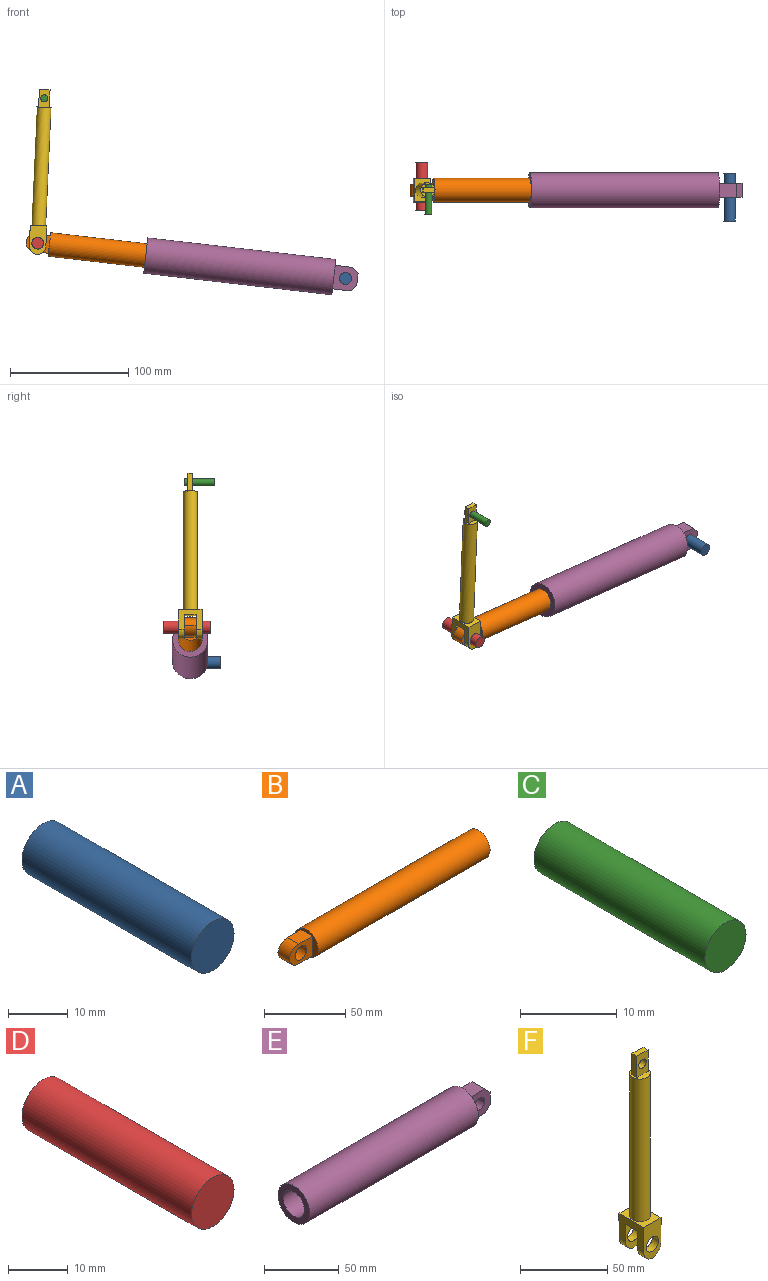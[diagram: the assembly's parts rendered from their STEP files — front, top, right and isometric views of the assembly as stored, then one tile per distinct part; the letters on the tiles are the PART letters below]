
ASSEMBLY  parts=6 mates=6
PART A: 3 faces, bbox 10x40x10 mm
  f0: cylinder r=5mm len=40mm, axis (0,1,0), area 1256.6mm2, adj f1,f2
  f1: plane 10x10mm, normal (0,-1,0), area 78.5mm2, adj f0
  f2: plane 10x10mm, normal (0,1,0), area 78.5mm2, adj f0
PART B: 10 faces, bbox 170x20x20 mm
  f0: plane 20x20mm, normal (-1,0,0), area 164.2mm2, adj f1,f3,f4,f5,f6
  f1: cylinder r=10mm len=150mm, axis (-1,0,0), area 9424.8mm2, adj f0,f2
  f2: plane 20x20mm, normal (1,0,0), area 314.2mm2, adj f1
  f3: plane 19.98x15mm, normal (0,-1,0), area 194mm2, adj f0,f4,f6,f7,f8,f9
  f4: plane 12x10mm, normal (0,0,1), area 120mm2, adj f0,f3,f5,f9
  f5: plane 19.98x15mm, normal (0,1,0), area 194mm2, adj f0,f4,f6,f7,f8,f9
  f6: plane 12x10mm, normal (0,0,-1), area 120mm2, adj f0,f3,f5,f8
  f7: cylinder r=5mm len=10mm, axis (0,-1,0), area 314.2mm2, adj f3,f5
  f8: cylinder r=8mm len=10mm, axis (0,1,0), area 120.7mm2, adj f3,f5,f6,f9
  f9: cylinder r=8mm len=10mm, axis (0,-1,0), area 120.7mm2, adj f3,f4,f5,f8
PART C: 3 faces, bbox 6x25x6 mm
  f0: cylinder r=3mm len=25mm, axis (0,1,0), area 471.2mm2, adj f1,f2
  f1: plane 6x6mm, normal (0,-1,0), area 28.3mm2, adj f0
  f2: plane 6x6mm, normal (0,1,0), area 28.3mm2, adj f0
PART D: 3 faces, bbox 10x40x10 mm
  f0: cylinder r=5mm len=40mm, axis (0,1,0), area 1256.6mm2, adj f1,f2
  f1: plane 10x10mm, normal (0,-1,0), area 78.5mm2, adj f0
  f2: plane 10x10mm, normal (0,1,0), area 78.5mm2, adj f0
PART E: 13 faces, bbox 180x30x30 mm
  f0: cylinder r=10mm len=150mm, axis (-1,0,0), area 9424.8mm2, adj f2,f3
  f1: cylinder r=15mm len=160mm, axis (-1,0,0), area 15079.6mm2, adj f2,f4
  f2: plane 30x30mm, normal (-1,0,0), area 392.7mm2, adj f0,f1
  f3: plane 20x20mm, normal (-1,0,0), area 314.2mm2, adj f0
  f4: plane 30x30mm, normal (1,0,0), area 466.9mm2, adj f1,f5,f6,f7,f8
  f5: plane 20x20mm, normal (0,-1,0), area 296.5mm2, adj f4,f6,f8,f9,f10,f11,f12
  f6: plane 15x12mm, normal (0,0,-1), area 180mm2, adj f4,f5,f7,f11
  f7: plane 20x20mm, normal (0,1,0), area 296.5mm2, adj f4,f6,f8,f9,f10,f11,f12
  f8: plane 15x12mm, normal (0,0,1), area 180mm2, adj f4,f5,f7,f12
  f9: plane 12x10mm, normal (1,0,0), area 120mm2, adj f5,f7,f11,f12
  f10: cylinder r=5mm len=12mm, axis (0,-1,0), area 377mm2, adj f5,f7
  f11: plane 12x5mm, normal (0.71,0,-0.71), area 84.9mm2, adj f5,f6,f7,f9
  f12: plane 12x5mm, normal (0.71,0,0.71), area 84.9mm2, adj f5,f7,f8,f9
PART F: 25 faces, bbox 14x20x139.9 mm
  f0: plane 12x12mm, normal (0,0,1), area 77.1mm2, adj f18,f19,f20,f21,f22
  f1: plane 19.94x14mm, normal (0,1,0), area 174mm2, adj f2,f4,f11,f13,f16,f17
  f2: plane 20.02x17mm, normal (-1,0,0), area 220.1mm2, adj f1,f3,f5,f7,f9,f10,f11,f14
  f3: plane 19.94x14mm, normal (0,-1,0), area 174mm2, adj f2,f4,f11,f13,f16,f17
  f4: plane 12x5mm, normal (1,0,0), area 60mm2, adj f1,f3,f11,f16
  f5: plane 24.94x14.03mm, normal (0,-1,0), area 244.2mm2, adj f2,f6,f8,f10,f11,f12,f14,f15
  f6: plane 12x5mm, normal (1,0,0), area 60mm2, adj f5,f7,f11,f15
  f7: plane 19.94x14mm, normal (0,1,0), area 174mm2, adj f2,f6,f11,f12,f14,f15
  f8: plane 20.02x5mm, normal (1,0,0), area 100.1mm2, adj f5,f9,f10,f11
  f9: plane 14.03x5mm, normal (0,1,0), area 70.2mm2, adj f2,f8,f10,f11
  f10: plane 20.02x14.03mm, normal (0,0,1), area 167.8mm2, adj f2,f5,f8,f9,f18
  f11: plane 20.02x14.03mm, normal (0,0,-1), area 140.9mm2, adj f1,f2,f3,f4,f5,f6,f7,f8
  f12: cylinder r=5mm len=10mm, axis (0,1,0), area 157.1mm2, adj f5,f7
  f13: cylinder r=5mm len=10mm, axis (0,1,0), area 157.1mm2, adj f1,f3
  f14: cylinder r=8mm len=7.94mm, axis (0,-1,0), area 57.8mm2, adj f2,f5,f7,f15
  f15: cylinder r=8mm len=7.94mm, axis (0,1,0), area 57.8mm2, adj f5,f6,f7,f14
  f16: cylinder r=8mm len=7.94mm, axis (0,1,0), area 57.8mm2, adj f1,f3,f4,f17
  f17: cylinder r=8mm len=7.94mm, axis (0,-1,0), area 57.8mm2, adj f1,f2,f3,f16
  f18: cylinder r=6mm len=100mm, axis (0,0,-1), area 3769.9mm2, adj f0,f10
  f19: plane 15x9mm, normal (0,1,0), area 106.7mm2, adj f0,f20,f22,f23,f24
  f20: plane 15x4mm, normal (-1,0,0), area 60mm2, adj f0,f19,f21,f23
  f21: plane 15x9mm, normal (0,-1,0), area 106.7mm2, adj f0,f20,f22,f23,f24
  f22: plane 15x4mm, normal (1,0,0), area 60mm2, adj f0,f19,f21,f23
  f23: plane 9x4mm, normal (0,0,1), area 36mm2, adj f19,f20,f21,f22
  f24: cylinder r=3mm len=6mm, axis (0,1,0), area 75.4mm2, adj f19,f21
PLACE A t=(-37.8,26.98,-41.55)mm fixed
PLACE B rot(axis=(0,1,0),6.5deg) t=(-43.61,32.98,-21.38)mm
PLACE C t=(-37.49,26.98,-11.82)mm fixed
PLACE D t=(-43.06,40.98,-11.69)mm
PLACE E rot(axis=(0,1,0),6.5deg) t=(-36.7,32.98,-22.17)mm
PLACE F rot(axis=(0,1,0),2.6deg) t=(-43.15,32.98,-15.56)mm
MATE revolute B.f7 <-> F.f12  axis (0,-1,0) through (-128.06,27.98,-11.69)mm
MATE cylindrical C.f0 <-> F.f24  axis (0,1,0) through (-122.48,24.98,110.68)mm
MATE cylindrical D.f0 <-> F.f12  axis (0,1,0) through (-128.06,35.98,-11.69)mm
MATE slider B.f1 <-> E.f0  axis (-0.99,0,0.11) through (-43.61,32.98,-21.38)mm
MATE cylindrical D.f0 <-> B.f7  axis (0,1,0) through (-128.06,35.98,-11.69)mm
MATE revolute A.f0 <-> E.f10  axis (0,1,0) through (132.2,26.98,-41.55)mm
